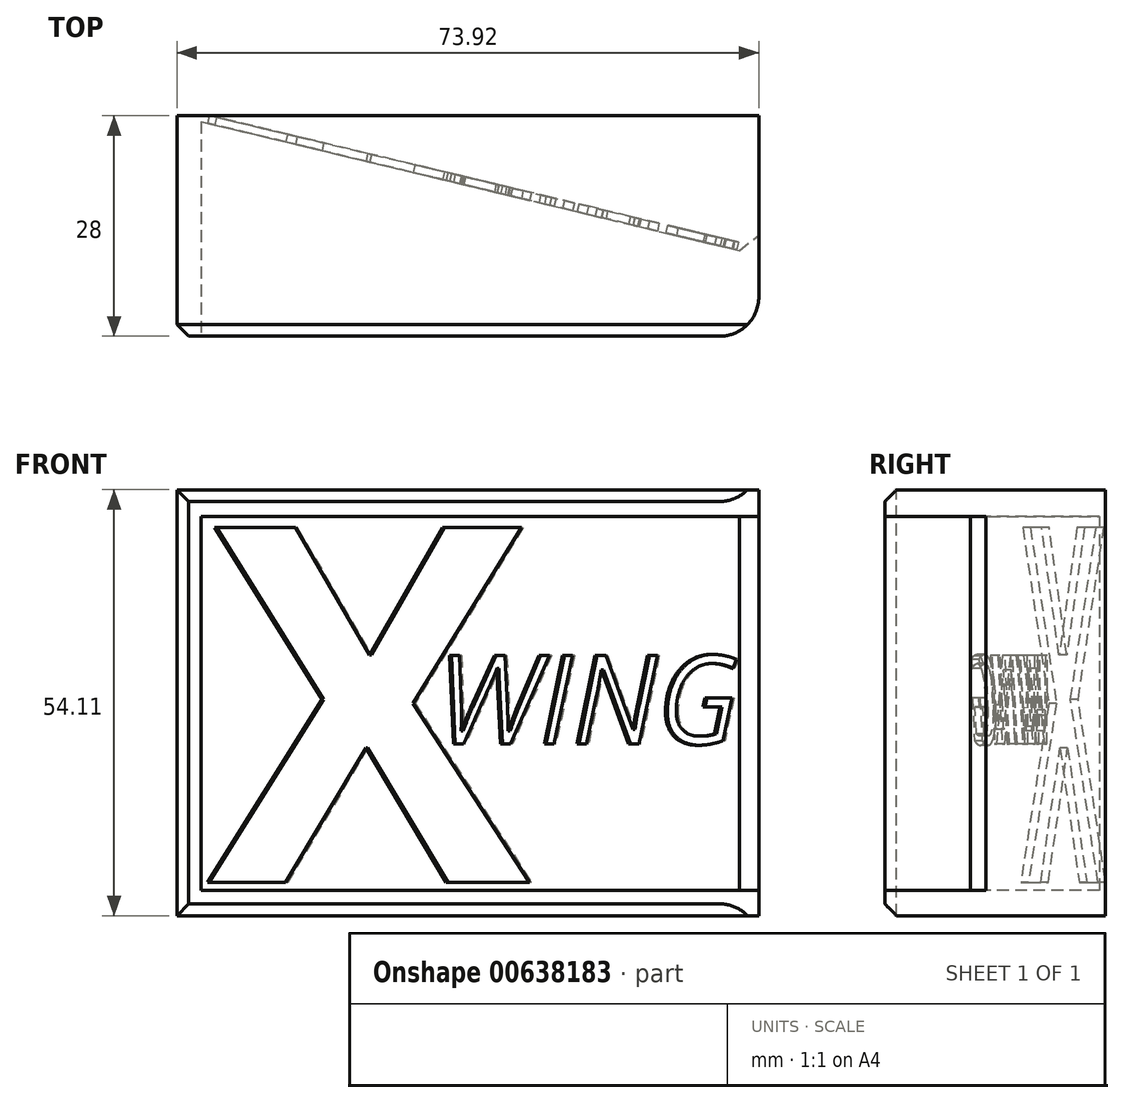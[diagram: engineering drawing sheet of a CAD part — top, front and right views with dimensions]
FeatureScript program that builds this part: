
annotation { "Feature Type Name" : "Feature", "Feature Type Description" : "" }
export const myFeature = defineFeature(function(context is Context, id is Id, definition is map)
    precondition{}
    {
        {
            var Q0;
            Q0=qCreatedBy(makeId("Front.planeOp"),FACE);
            var sketch = newSketch(context, id + "F0", { "sketchPlane" : qUnion([Q0])});
            skLineSegment(sketch, "E0", {"start": v(31.06, 0) * mm, "end": v(-42.86, 0) * mm});
            skLineSegment(sketch, "E1", {"start": v(-42.86, 0) * mm, "end": v(-42.86, 54.1) * mm});
            skLineSegment(sketch, "E2", {"start": v(-42.86, 54.1) * mm, "end": v(31.06, 54.1) * mm});
            skLineSegment(sketch, "E3", {"start": v(31.06, 54.1) * mm, "end": v(31.06, 50.73) * mm});
            skLineSegment(sketch, "E4", {"start": v(31.06, 50.73) * mm, "end": v(-39.77, 50.73) * mm});
            skLineSegment(sketch, "E5", {"start": v(-39.77, 50.73) * mm, "end": v(-39.77, 3.23) * mm});
            skLineSegment(sketch, "E6", {"start": v(-39.77, 3.23) * mm, "end": v(31.06, 3.23) * mm});
            skLineSegment(sketch, "E7", {"start": v(31.06, 3.23) * mm, "end": v(31.06, 0) * mm});
            skSolve(sketch);
        }
        {
            var Q0;
            Q0 = qSketchRegion(id + "F0", true);
            extrude(context, id + "F1", {"entities" : qUnion([Q0]), "oppositeDirection" : true, "depth" : 28 * mm, "offsetDistance" : 25 * mm});
        }
        {
            var Q0;
            Q0=makeQuery(id+"F1.opExtrude","SWEPT_FACE",FACE,{"disambiguationData":[OSD([sQuery(id+"F0.wireOp",EDGE,"E0")])]});
            var sketch = newSketch(context, id + "F2", { "sketchPlane" : qUnion([Q0])});
            skLineSegment(sketch, "E8", {"start": v(-42.86, -28) * mm, "end": v(31.06, -10.29) * mm});
            skLineSegment(sketch, "E9", {"start": v(31.06, -10.29) * mm, "end": v(31.06, -28) * mm});
            skLineSegment(sketch, "E10", {"start": v(31.06, -28) * mm, "end": v(-42.86, -28) * mm});
            skSolve(sketch);
        }
        {
            var Q0;
            Q0=makeQuery(id+"F2.imprint","IMPRINT",FACE,{"disambiguationData":[TD([[makeQuery(id+"F2.imprint","IMPRINT",EDGE,{"derivedFrom":sQuery(id+"F2.wireOp",EDGE,"E8")}),-1.0]])]});
            extrude(context, id + "F3", {"entities" : qUnion([Q0]), "operationType" : NewBodyOperationType.ADD, "oppositeDirection" : true, "depth" : 54 * mm, "offsetDistance" : 25 * mm});
        }
        {
            var Q0;
            Q0=makeQuery(id+"F1.opExtrude","CAP_EDGE",EDGE,{"disambiguationData":[OSD([sQuery(id+"F0.wireOp",EDGE,"E0")])],"isStart":true});
            var Q1;
            Q1=makeQuery(id+"F1.opExtrude","CAP_EDGE",EDGE,{"disambiguationData":[OSD([sQuery(id+"F0.wireOp",EDGE,"E1")])],"isStart":true});
            var Q2;
            Q2=makeQuery(id+"F1.opExtrude","CAP_EDGE",EDGE,{"disambiguationData":[OSD([sQuery(id+"F0.wireOp",EDGE,"E2")])],"isStart":true});
            chamfer(context, id + "F4", {"entities" : qUnion([Q0, Q1, Q2]), "width" : 1.5 * mm, "tangentPropagation" : true});
        }
        {
            var Q0;
            Q0=makeQuery(id+"F1.opExtrude","CAP_EDGE",EDGE,{"disambiguationData":[OSD([sQuery(id+"F0.wireOp",EDGE,"E3")])],"isStart":true});
            var Q1;
            Q1=makeQuery(id+"F1.opExtrude","CAP_EDGE",EDGE,{"disambiguationData":[OSD([sQuery(id+"F0.wireOp",EDGE,"E7")])],"isStart":true});
            fillet(context, id + "F5", {"entities" : qUnion([Q0, Q1]), "radius" : 5 * mm, "tangentPropagation" : true, "allowEdgeOverflow" : false});
        }
        {
            var Q0;
            Q0=makeQuery(id+"F3.opExtrude","SWEPT_EDGE",EDGE,{"disambiguationData":[OSD([sQuery(id+"F0.wireOp",EDGE,"E0"),sQuery(id+"F0.wireOp",EDGE,"E7"),sQuery(id+"F2.wireOp",EDGE,"E8"),sQuery(id+"F2.wireOp",EDGE,"E9")])]});
            chamfer(context, id + "F6", {"entities" : qUnion([Q0]), "width" : 2 * mm, "tangentPropagation" : true});
        }
        {
            var Q0;
            Q0=makeQuery(id+"F3.opExtrude","SWEPT_FACE",FACE,{"disambiguationData":[OSD([sQuery(id+"F2.wireOp",EDGE,"E8")])]});
            var sketch = newSketch(context, id + "F7", { "sketchPlane" : qUnion([Q0])});
            skText(sketch, "E11", { "text": "X", "fontName": "OpenSans-Bold.ttf"});
            const initialGuessF7  = {"E11": [-0.04422, 0.00426, 1, 0, 0.04542]};
            skSetInitialGuess(sketch, initialGuessF7);
            skSolve(sketch);
        }
        {
            var Q0;
            Q0=makeQuery(id+"F7.imprint","IMPRINT",FACE,{"disambiguationData":[TD([[makeQuery(id+"F7.imprint","IMPRINT",EDGE,{"derivedFrom":sQuery(id+"F7.wireOp",EDGE,"E11.sketch_text.stroke-0")}),1.0]])]});
            var sketch = newSketch(context, id + "F8", { "sketchPlane" : qUnion([Q0])});
            skText(sketch, "E12", { "text": "WING", "fontName": "OpenSans-Italic.ttf"});
            const initialGuessF8  = {"E12": [-0.01429, 0.0218, 1, 0, 0.01133]};
            skSetInitialGuess(sketch, initialGuessF8);
            skSolve(sketch);
        }
        {
            var Q0;
            Q0 = qSketchRegion(id + "F8", true);
            extrude(context, id + "F9", {"entities" : qUnion([Q0]), "operationType" : NewBodyOperationType.REMOVE, "oppositeDirection" : true, "depth" : 1 * mm, "offsetDistance" : 25 * mm});
        }
        {
            var Q0;
            Q0=makeQuery(id+"F7.imprint","IMPRINT",FACE,{"disambiguationData":[TD([[makeQuery(id+"F7.imprint","IMPRINT",EDGE,{"derivedFrom":sQuery(id+"F7.wireOp",EDGE,"E11.sketch_text.stroke-0")}),-1.0]])]});
            extrude(context, id + "F10", {"entities" : qUnion([Q0]), "operationType" : NewBodyOperationType.REMOVE, "oppositeDirection" : true, "depth" : 1 * mm, "offsetDistance" : 25 * mm});
        }
    });
